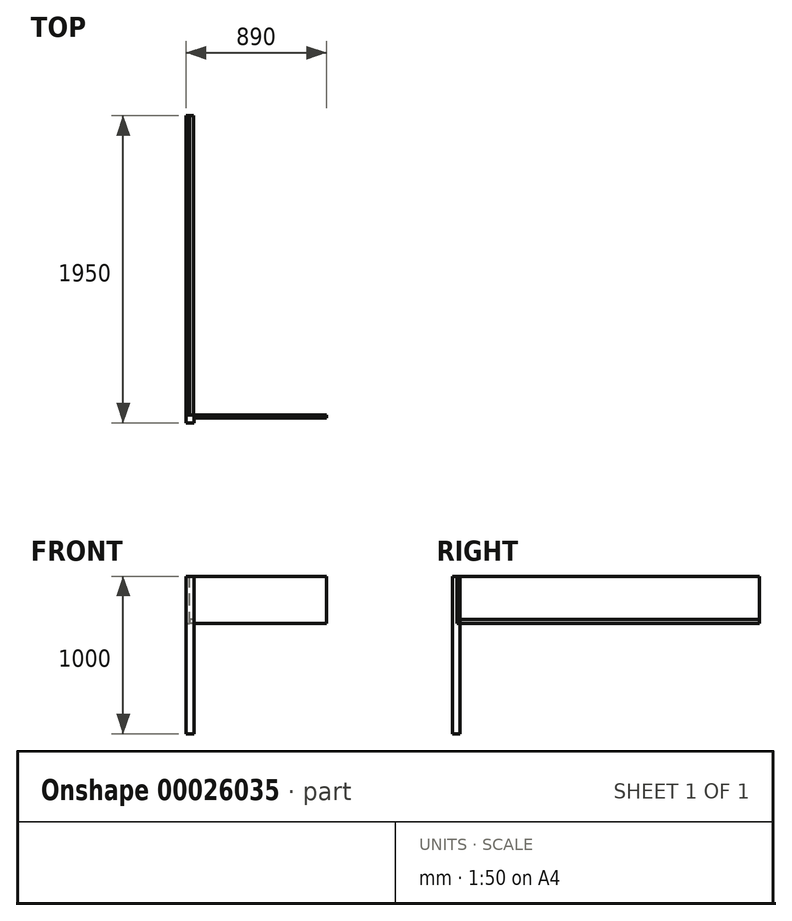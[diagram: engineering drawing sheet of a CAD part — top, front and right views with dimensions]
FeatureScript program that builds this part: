
annotation { "Feature Type Name" : "Feature", "Feature Type Description" : "" }
export const myFeature = defineFeature(function(context is Context, id is Id, definition is map)
    precondition{}
    {
        {
            var Q0;
            Q0=qCreatedBy(makeId("Front.planeOp"),FACE);
            var sketch = newSketch(context, id + "F0", { "sketchPlane" : qUnion([Q0])});
            skLineSegment(sketch, "E0.bottom", {"start": v(0, 0) * mm, "end": v(20, 0) * mm});
            skLineSegment(sketch, "E0.top", {"start": v(0, 300) * mm, "end": v(20, 300) * mm});
            skLineSegment(sketch, "E0.left", {"start": v(0, 0) * mm, "end": v(0, 300) * mm});
            skLineSegment(sketch, "E0.right", {"start": v(20, 0) * mm, "end": v(20, 300) * mm});
            skSolve(sketch);
        }
        {
            var Q0;
            Q0 = qSketchRegion(id + "F0", true);
            extrude(context, id + "F1", {"entities" : qUnion([Q0]), "depth" : 1900 * mm});
        }
        {
            var Q0;
            Q0=makeQuery(id+"F1.opExtrude","CAP_FACE",FACE,{"disambiguationData":[OSD([sQuery(id+"F0.wireOp",EDGE,"E0.bottom"),sQuery(id+"F0.wireOp",EDGE,"E0.top"),sQuery(id+"F0.wireOp",EDGE,"E0.left"),sQuery(id+"F0.wireOp",EDGE,"E0.right")])],"isStart":false});
            var sketch = newSketch(context, id + "F2", { "sketchPlane" : qUnion([Q0])});
            skLineSegment(sketch, "E1.bottom", {"start": v(20, 0) * mm, "end": v(45, 0) * mm});
            skLineSegment(sketch, "E1.top", {"start": v(20, 25) * mm, "end": v(45, 25) * mm});
            skLineSegment(sketch, "E1.left", {"start": v(20, 0) * mm, "end": v(20, 25) * mm});
            skLineSegment(sketch, "E1.right", {"start": v(45, 0) * mm, "end": v(45, 25) * mm});
            skSolve(sketch);
        }
        {
            var Q0;
            Q0=makeQuery(id+"F2.imprint","IMPRINT",FACE,{"disambiguationData":[TD([[makeQuery(id+"F2.imprint","IMPRINT",EDGE,{"derivedFrom":sQuery(id+"F2.wireOp",EDGE,"E1.bottom")}),1.0]])]});
            var Q1;
            Q1=makeQuery(id+"F1.opExtrude","CAP_FACE",FACE,{"disambiguationData":[OSD([sQuery(id+"F0.wireOp",EDGE,"E0.bottom"),sQuery(id+"F0.wireOp",EDGE,"E0.top"),sQuery(id+"F0.wireOp",EDGE,"E0.left"),sQuery(id+"F0.wireOp",EDGE,"E0.right")])],"isStart":true});
            extrude(context, id + "F3", {"entities" : qUnion([Q0]), "endBound" : BoundingType.UP_TO_SURFACE, "oppositeDirection" : true, "endBoundEntityFace" : qUnion([Q1]), "depth" : 25 * mm});
        }
        {
            var Q0;
            Q0=makeQuery(id+"F1.opExtrude","SWEPT_FACE",FACE,{"disambiguationData":[OSD([sQuery(id+"F0.wireOp",EDGE,"E0.top")])]});
            var sketch = newSketch(context, id + "F4", { "sketchPlane" : qUnion([Q0])});
            skLineSegment(sketch, "E2.bottom", {"start": v(0, -1900) * mm, "end": v(50, -1900) * mm});
            skLineSegment(sketch, "E2.top", {"start": v(0, -1950) * mm, "end": v(50, -1950) * mm});
            skLineSegment(sketch, "E2.left", {"start": v(0, -1900) * mm, "end": v(0, -1950) * mm});
            skLineSegment(sketch, "E2.right", {"start": v(50, -1900) * mm, "end": v(50, -1950) * mm});
            skSolve(sketch);
        }
        {
            var Q0;
            Q0 = qSketchRegion(id + "F4", true);
            extrude(context, id + "F5", {"entities" : qUnion([Q0]), "oppositeDirection" : true, "depth" : 1000 * mm});
        }
        {
            var Q0;
            Q0=makeQuery(id+"F5.opExtrude","SWEPT_BODY",BODY,{"disambiguationData":[OSD([sQuery(id+"F4.wireOp",EDGE,"E2.bottom"),sQuery(id+"F4.wireOp",EDGE,"E2.top"),sQuery(id+"F4.wireOp",EDGE,"E2.left"),sQuery(id+"F4.wireOp",EDGE,"E2.right")])]});
            transform(context, id + "F6", {"entities" : qUnion([Q0]), "transformType" : TransformType.TRANSLATION_3D, "dx" : 0 * mm, "dy" : 0 * mm, "dz" : 0 * mm, "makeCopy" : true});
        }
        {
            var Q0;
            Q0=makeQuery(id+"F6.opPattern","COPY",BODY,{"derivedFrom":makeQuery(id+"F5.opExtrude","SWEPT_BODY",BODY,{"disambiguationData":[OSD([sQuery(id+"F4.wireOp",EDGE,"E2.bottom"),sQuery(id+"F4.wireOp",EDGE,"E2.top"),sQuery(id+"F4.wireOp",EDGE,"E2.left"),sQuery(id+"F4.wireOp",EDGE,"E2.right")])]}),"instanceName":"1"});
            deleteBodies(context, id + "F7", {"entities" : qUnion([Q0])});
        }
        {
            var Q0;
            Q0=makeQuery(id+"F5.opExtrude","SWEPT_FACE",FACE,{"disambiguationData":[OSD([sQuery(id+"F4.wireOp",EDGE,"E2.right")])]});
            var sketch = newSketch(context, id + "F8", { "sketchPlane" : qUnion([Q0])});
            skLineSegment(sketch, "E3.bottom", {"start": v(-1900, 300) * mm, "end": v(-1920, 300) * mm});
            skLineSegment(sketch, "E3.top", {"start": v(-1900, 0) * mm, "end": v(-1920, 0) * mm});
            skLineSegment(sketch, "E3.left", {"start": v(-1900, 300) * mm, "end": v(-1900, 0) * mm});
            skLineSegment(sketch, "E3.right", {"start": v(-1920, 300) * mm, "end": v(-1920, 0) * mm});
            skSolve(sketch);
        }
        {
            var Q0;
            Q0=makeQuery(id+"F8.imprint","IMPRINT",FACE,{"disambiguationData":[TD([[makeQuery(id+"F8.imprint","IMPRINT",EDGE,{"derivedFrom":sQuery(id+"F8.wireOp",EDGE,"E3.bottom")}),1.0]])]});
            extrude(context, id + "F9", {"entities" : qUnion([Q0]), "depth" : 840 * mm});
        }
    });
